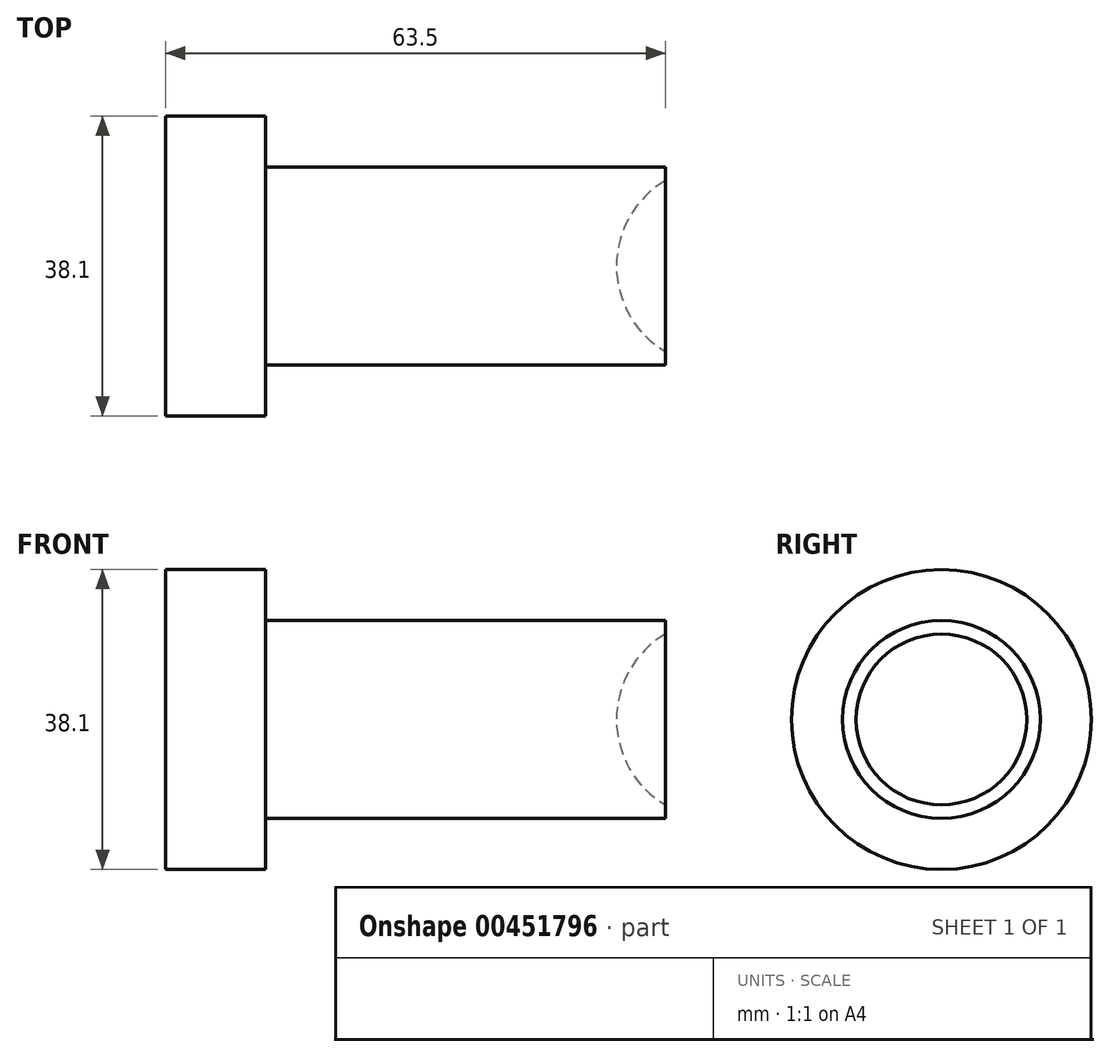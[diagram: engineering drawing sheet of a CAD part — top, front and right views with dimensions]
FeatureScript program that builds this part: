
annotation { "Feature Type Name" : "Feature", "Feature Type Description" : "" }
export const myFeature = defineFeature(function(context is Context, id is Id, definition is map)
    precondition{}
    {
        {
            var Q0;
            Q0=qCreatedBy(makeId("Front.planeOp"),FACE);
            var sketch = newSketch(context, id + "F0", { "sketchPlane" : qUnion([Q0])});
            skLineSegment(sketch, "E0.bottom", {"start": v(-12.7, 19.05) * mm, "end": v(0, 19.05) * mm});
            skLineSegment(sketch, "E0.top", {"start": v(-12.7, 0) * mm, "end": v(0, 0) * mm});
            skLineSegment(sketch, "E0.left", {"start": v(-12.7, 19.05) * mm, "end": v(-12.7, 0) * mm});
            skLineSegment(sketch, "E0.right", {"start": v(0, 19.05) * mm, "end": v(0, 12.57) * mm});
            skLineSegment(sketch, "E1.bottom", {"start": v(0, 12.57) * mm, "end": v(50.8, 12.57) * mm});
            skLineSegment(sketch, "E1.top", {"start": v(0, 0) * mm, "end": v(50.8, 0) * mm});
            skLineSegment(sketch, "E1.right", {"start": v(50.8, 12.57) * mm, "end": v(50.8, 0) * mm});
            skSolve(sketch);
        }
        {
            var Q0;
            Q0 = qSketchRegion(id + "F0", true);
            var Q1;
            Q1=sQuery(id+"F0.wireOp",EDGE,"E1.top");
            revolve(context, id + "F1", {"entities" : qUnion([Q0]), "axis" : qUnion([Q1]), "revolveType" : RevolveType.FULL});
        }
        {
            var Q0;
            Q0=qCreatedBy(makeId("Front.planeOp"),FACE);
            var sketch = newSketch(context, id + "F2", { "sketchPlane" : qUnion([Q0])});
            skArc(sketch, "E2", {"start": v(57.15, 12.57) * mm, "mid": v(44.58, 0) * mm, "end": v(57.15, -12.57) * mm});
            skLineSegment(sketch, "E3", {"start": v(57.15, 0) * mm, "end": v(57.15, -12.57) * mm});
            skLineSegment(sketch, "E4", {"start": v(57.15, -12.57) * mm, "end": v(57.15, 12.57) * mm});
            skSolve(sketch);
        }
        {
            var Q0;
            Q0 = qSketchRegion(id + "F2", true);
            var Q1;
            Q1=sQuery(id+"F2.wireOp",EDGE,"E4");
            revolve(context, id + "F3", {"operationType" : NewBodyOperationType.REMOVE, "entities" : qUnion([Q0]), "axis" : qUnion([Q1]), "revolveType" : RevolveType.FULL, "oppositeDirection" : true});
        }
    });
